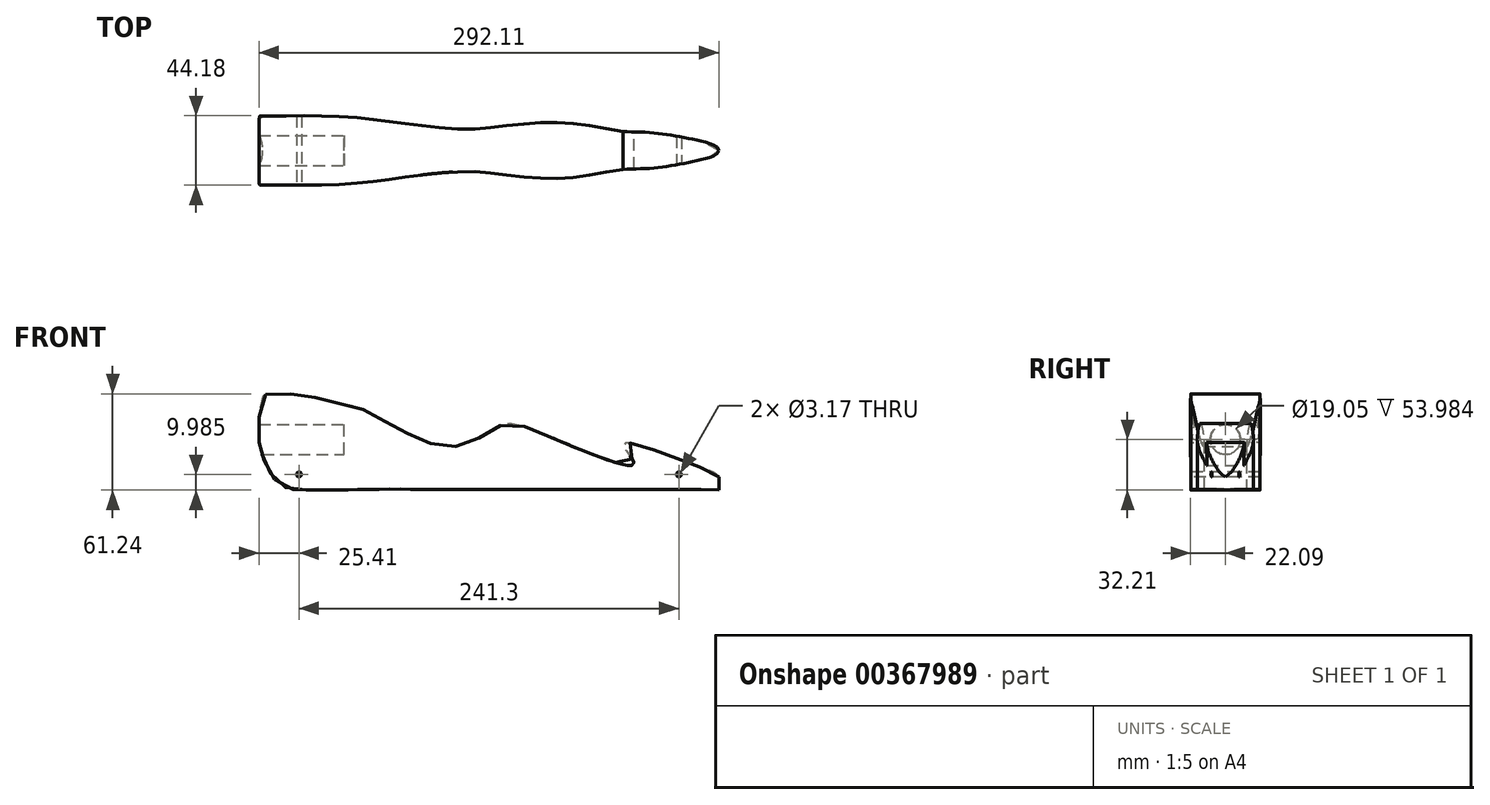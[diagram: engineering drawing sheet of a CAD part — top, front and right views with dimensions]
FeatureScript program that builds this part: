
annotation { "Feature Type Name" : "Feature", "Feature Type Description" : "" }
export const myFeature = defineFeature(function(context is Context, id is Id, definition is map)
    precondition{}
    {
        {
            var Q0;
            Q0=qCreatedBy(makeId("Front.planeOp"),FACE);
            var sketch = newSketch(context, id + "F0", { "sketchPlane" : qUnion([Q0])});
            skLineSegment(sketch, "E0.bottom", {"start": v(-146.05, 31.75) * mm, "end": v(146.05, 31.75) * mm, "construction": true});
            skLineSegment(sketch, "E0.top", {"start": v(-146.05, -31.75) * mm, "end": v(146.05, -31.75) * mm, "construction": true});
            skLineSegment(sketch, "E0.right", {"start": v(146.05, 31.75) * mm, "end": v(146.05, -31.75) * mm, "construction": true});
            skFitSpline(sketch, "E1", {"points": [v(-146.05, -1.84) * mm, v(-146.05, 0) * mm, v(-146.05, 9.53) * mm, v(-144.08, 26.83) * mm, v(-140.3, 28.73) * mm, v(-126.46, 28.82) * mm, v(-105.08, 25.54) * mm, v(-89.73, 21.7) * mm, v(-79.86, 19.2) * mm, v(-25.16, -4.53) * mm, v(7.2, 8.94) * mm, v(31.34, 4.77) * mm, v(92.09, -15.65) * mm, v(85.25, -3.16) * mm, v(115.33, -10.63) * mm, v(140.2, -19.79) * mm, v(146.05, -23.87) * mm, v(146.19, -28.92) * mm, v(146.4, -31.77) * mm, v(143.75, -32.08) * mm, v(115.43, -31.75) * mm, v(90.9, -31.75) * mm, v(68.3, -31.75) * mm, v(46.62, -31.75) * mm, v(19.15, -31.75) * mm, v(-6.94, -31.75) * mm, v(-28.08, -31.75) * mm, v(-39.16, -31.78) * mm, v(-49.11, -31.64) * mm, v(-62.12, -31.54) * mm, v(-113.63, -32.2) * mm, v(-136.24, -25.36) * mm, v(-146.05, -1.84) * mm]});
            skLineSegment(sketch, "E2.bottom", {"start": v(-146.05, 9.52) * mm, "end": v(-95.25, 9.52) * mm, "construction": true});
            skLineSegment(sketch, "E2.top", {"start": v(-137.42, -9.52) * mm, "end": v(-95.25, -9.52) * mm, "construction": true});
            skLineSegment(sketch, "E2.right", {"start": v(-95.25, 9.52) * mm, "end": v(-95.25, -9.52) * mm, "construction": true});
            skLineSegment(sketch, "E3", {"start": v(-146.05, 31.75) * mm, "end": v(-146.05, -31.75) * mm, "construction": true});
            skSolve(sketch);
        }
        {
            var Q0;
            Q0=qCreatedBy(makeId("Top.planeOp"),FACE);
            var sketch = newSketch(context, id + "F1", { "sketchPlane" : qUnion([Q0])});
            skLineSegment(sketch, "E4.bottom", {"start": v(-146.05, 22.23) * mm, "end": v(146.05, 22.23) * mm, "construction": true});
            skLineSegment(sketch, "E4.top", {"start": v(-146.05, -22.23) * mm, "end": v(146.05, -22.23) * mm, "construction": true});
            skLineSegment(sketch, "E4.left", {"start": v(-146.05, 22.23) * mm, "end": v(-146.05, -22.23) * mm, "construction": true});
            skLineSegment(sketch, "E4.right", {"start": v(146.05, 22.23) * mm, "end": v(146.05, -22.23) * mm, "construction": true});
            skLineSegment(sketch, "E5", {"start": v(-146.05, 0) * mm, "end": v(146.05, 0) * mm, "construction": true});
            skFitSpline(sketch, "E6", {"points": [v(-146.05, 0) * mm, v(-146.05, 20) * mm, v(-145.68, 21.84) * mm, v(-141.76, 21.98) * mm, v(-93.94, 21.5) * mm, v(-42.16, 15.57) * mm, v(-9.93, 13.52) * mm, v(13.27, 15.88) * mm, v(52.62, 17.3) * mm, v(82.76, 12.37) * mm, v(101.63, 11.4) * mm, v(127.6, 7.47) * mm, v(146.05, 0) * mm], "startDerivative": vector(0, 335.54) * mm, "endDerivative": vector(0, -145.95) * mm});
            skFitSpline(sketch, "E7.MirrorCS", {"points": [v(-146.05, 0) * mm, v(-146.05, -20) * mm, v(-145.68, -21.84) * mm, v(-141.76, -21.98) * mm, v(-93.94, -21.5) * mm, v(-42.16, -15.57) * mm, v(-9.93, -13.52) * mm, v(13.27, -15.88) * mm, v(52.62, -17.3) * mm, v(82.76, -12.37) * mm, v(101.63, -11.4) * mm, v(127.6, -7.47) * mm, v(146.05, 0) * mm], "startDerivative": vector(0, -335.54) * mm, "endDerivative": vector(0, 145.95) * mm});
            skLineSegment(sketch, "E8.MirrorCS", {"start": v(-146.05, -22.23) * mm, "end": v(146.05, -22.23) * mm});
            skSolve(sketch);
        }
        {
            var Q0;
            Q0=qCreatedBy(makeId("Right.planeOp"),FACE);
            var sketch = newSketch(context, id + "F2", { "sketchPlane" : qUnion([Q0])});
            skCircle(sketch, "E9", {"center": v(0, 0) * mm, "radius": 9.53 * mm});
            skSolve(sketch);
        }
        {
            var Q0;
            Q0=qCreatedBy(makeId("Front.planeOp"),FACE);
            var sketch = newSketch(context, id + "F3", { "sketchPlane" : qUnion([Q0])});
            skCircle(sketch, "E10", {"center": v(-120.65, -22.22) * mm, "radius": 1.59 * mm});
            skCircle(sketch, "E11", {"center": v(120.65, -22.23) * mm, "radius": 1.59 * mm});
            skSolve(sketch);
        }
        {
            var Q0;
            Q0=qSketchRegion(id+"F0",true);
            extrude(context, id + "F4", {"entities" : qUnion([Q0]), "depth" : 44.45 * mm, "symmetric" : true});
        }
        {
            var Q0;
            Q0=qSketchRegion(id+"F1",true);
            extrude(context, id + "F5", {"entities" : qUnion([Q0]), "operationType" : NewBodyOperationType.INTERSECT, "endBound" : BoundingType.THROUGH_ALL, "oppositeDirection" : true, "depth" : 60.96 * mm, "hasSecondDirection" : true, "secondDirectionBound" : BoundingType.THROUGH_ALL, "secondDirectionOppositeDirection" : false, "secondDirectionDepth" : 25.4 * mm});
        }
        {
            var Q0;
            Q0=qSketchRegion(id+"F2",true);
            extrude(context, id + "F6", {"entities" : qUnion([Q0]), "operationType" : NewBodyOperationType.REMOVE, "oppositeDirection" : true, "depth" : 152.4 * mm, "hasSecondDirection" : true, "secondDirectionOppositeDirection" : true, "secondDirectionDepth" : 92.07 * mm});
        }
        {
            var Q0;
            Q0=qSketchRegion(id+"F3",true);
            extrude(context, id + "F7", {"entities" : qUnion([Q0]), "operationType" : NewBodyOperationType.REMOVE, "oppositeDirection" : true, "depth" : 50.8 * mm, "symmetric" : true});
        }
    });
